# Revit family: ВВГФ-ВО_eng
name_source: partatom
category: Duct Accessories
units: mm (PartAtom-declared; Revit-internal decimal feet)

## family parameters
Always vertical = Yes
Cut with Voids When Loaded = No
Part Type = Attaches To
Round Connector Dimension = Use Diameter
Shared = No
Work Plane-Based = No

## types (11) — shared parameters
00_20_Manufacturer = Vents
00_20_Name = Flexible joint
Casing Material = Metal, painted, blue, matte RAL 5007
L = 260 mm  [stored 0.853018 ft]
Load Classification = HVAC
Maintenance zone material = <By Category>
Manufacturer = Vents
URL = https://ventilation-system.com
Width = 260 mm  [stored 0.853018 ft]
l = 130 mm  [stored 0.426509 ft]
l1 = 87 mm
t = 255 mm  [stored 0.836614 ft]
zero-valued in all types: Default Elevation

## per-type parameters (varying)
| type | D1 | D2 | Diameter | Dn | Dy | R1 | Weight | d | n |
| VVGF-VO-400 | 450 mm  [stored 1.47638 ft] | 490 mm  [stored 1.60761 ft] | 490 mm  [stored 1.60761 ft] | 410 mm  [stored 1.34514 ft] | 400 mm  [stored 1.31234 ft] | 225 mm  [stored 0.738189 ft] | 4.76 kg | 8 mm  [stored 0.0262467 ft] | 12 |
| VVGF-VO-450 | 500 mm  [stored 1.64042 ft] | 540 mm  [stored 1.77165 ft] | 540 mm  [stored 1.77165 ft] | 460 mm | 450 mm  [stored 1.47638 ft] | 250 mm  [stored 0.82021 ft] | 5.34 kg | 8 mm  [stored 0.0262467 ft] | 12 |
| VVGF-VO-500 | 560 mm  [stored 1.83727 ft] | 600 mm | 600 mm | 510 mm | 500 mm  [stored 1.64042 ft] | 280 mm  [stored 0.918635 ft] | 6.12 kg | 12 mm  [stored 0.0393701 ft] | 12 |
| VVGF-VO-560 | 620 mm  [stored 2.03412 ft] | 660 mm | 660 mm | 570 mm  [stored 1.87008 ft] | 560 mm  [stored 1.83727 ft] | 310 mm  [stored 1.01706 ft] | 6.83 kg | 12 mm  [stored 0.0393701 ft] | 12 |
| VVGF-VO-630 | 690 mm  [stored 2.26378 ft] | 730 mm  [stored 2.39501 ft] | 730 mm  [stored 2.39501 ft] | 640 mm  [stored 2.09974 ft] | 630 mm  [stored 2.06693 ft] | 345 mm  [stored 1.13189 ft] | 7.66 kg | 12 mm  [stored 0.0393701 ft] | 12 |
| VVGF-VO-710 | 770 mm  [stored 2.52625 ft] | 810 mm | 810 mm | 720 mm | 710 mm | 385 mm  [stored 1.26312 ft] | 8.60 kg | 12 mm  [stored 0.0393701 ft] | 16 |
| VVGF-VO-800 | 860 mm | 900 mm | 900 mm | 810 mm | 800 mm  [stored 2.62467 ft] | 430 mm | 9.67 kg | 12 mm  [stored 0.0393701 ft] | 16 |
| VVGF-VO-900 | 970 mm | 1015 mm | 1015 mm | 910 mm | 900 mm | 485 mm  [stored 1.59121 ft] | 11.40 kg | 15 mm  [stored 0.0492126 ft] | 16 |
| VVGF-VO-1000 | 1070 mm | 1115 mm | 1115 mm | 1010 mm | 1000 mm | 535 mm  [stored 1.75525 ft] | 12.64 kg | 15 mm  [stored 0.0492126 ft] | 16 |
| VVGF-VO-1120 | 1190 mm | 1270 mm | 1270 mm | 1130 mm | 1120 mm | 595 mm  [stored 1.9521 ft] | 15.73 kg | 15 mm  [stored 0.0492126 ft] | 20 |
| VVGF-VO-1250 | 1320 mm | 1400 mm | 1400 mm | 1260 mm | 1250 mm | 660 mm | 17.52 kg | 15 mm  [stored 0.0492126 ft] | 20 |

note: column(s) folded — value = type name in every type: 00_20_Type

note: [stored X ft] marks values corroborated as IEEE doubles in the binary element streams (Revit-internal decimal feet)
